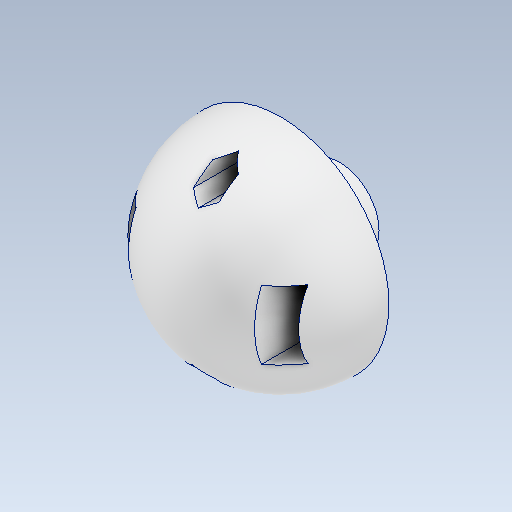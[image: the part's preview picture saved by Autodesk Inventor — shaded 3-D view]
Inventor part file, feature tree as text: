
AUTODESK INVENTOR PART (.ipt)
format: ipt  version: 2021 (Build 250183000, 183)  size: 166,912 bytes
history: native  units: mm
features: sketch x4, other x3
ambient origin geometry x8: Origin, YZ Plane, XZ Plane, XY Plane, X Axis, Y Axis, Z Axis, Center Point
bodies: Solid1 (feature_tree)
feature tree (7):
  other  "Rotatory Hinge 1.ipt"
  other  "Solid1::Rotatory Hinge 1.ipt"
  other  "TaggingFeature1"
  sketch  "Sketch1"  dims[d0=10.0mm]
  sketch  "Sketch2"
  sketch  "Sketch3"
  sketch  "Sketch4"
